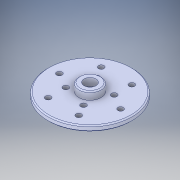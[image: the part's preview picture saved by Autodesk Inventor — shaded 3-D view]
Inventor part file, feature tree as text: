
AUTODESK INVENTOR PART (.ipt)
format: ipt  version: 2018 (Build 220112000, 112)  size: 154,112 bytes
history: native  units: in
note: dims shown in document units (in); Inventor stores cm internally (conversion verified against a paired STEP export)
features: chamfer x1
ambient origin geometry x8: Origin, YZ Plane, XZ Plane, XY Plane, X Axis, Y Axis, Z Axis, Center Point
bodies: Solid1 (feature_tree)
feature tree (1):
  chamfer  "Chamfer1"  [1 undecoded]
note: 1 required parameter value undecoded (feature->parameter linkage not recoverable at this tier; creation-order binding heuristic only, values carry confidence <= 0.55)
